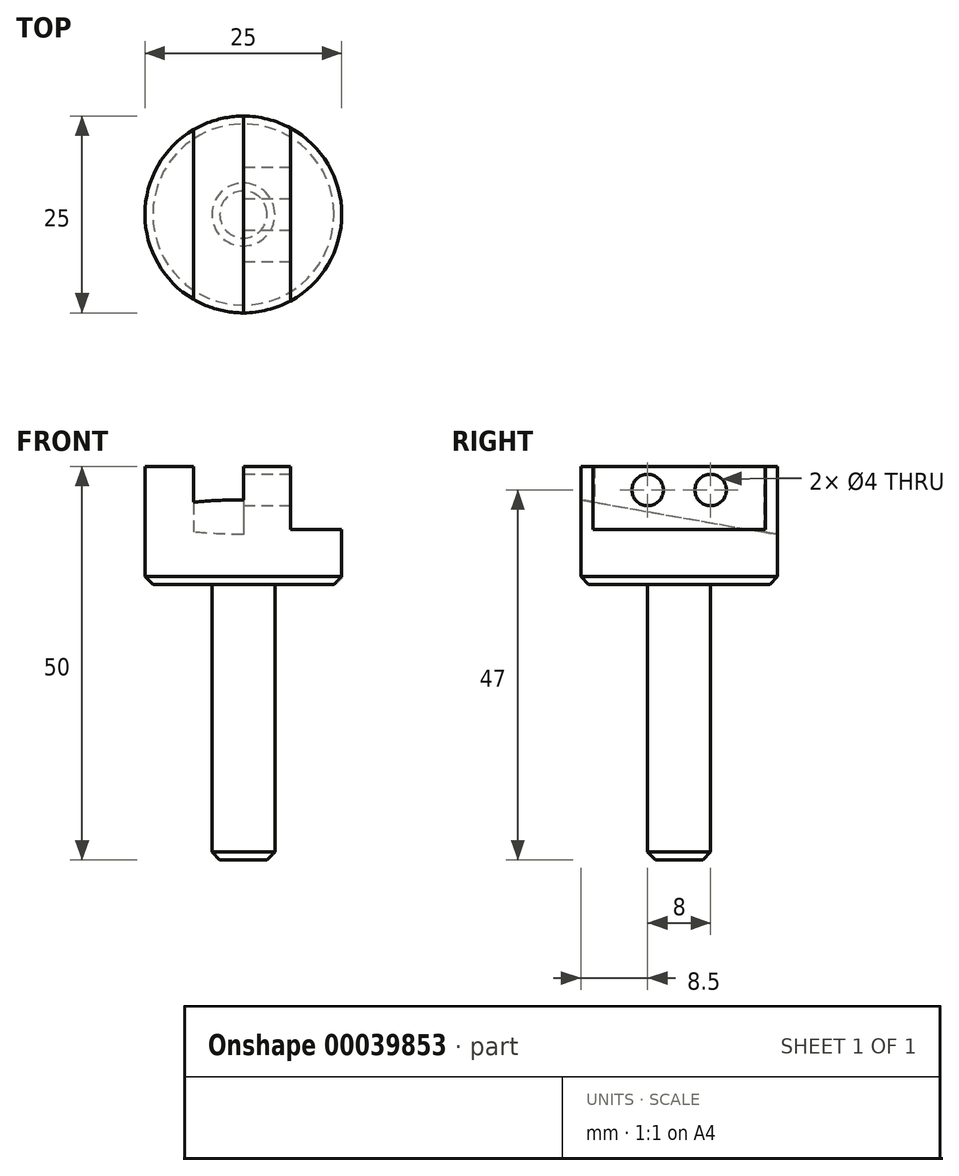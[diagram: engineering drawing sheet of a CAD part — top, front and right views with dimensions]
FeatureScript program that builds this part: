
annotation { "Feature Type Name" : "Feature", "Feature Type Description" : "" }
export const myFeature = defineFeature(function(context is Context, id is Id, definition is map)
    precondition{}
    {
        {
            var Q0;
            Q0=qCreatedBy(makeId("Top.planeOp"),FACE);
            var sketch = newSketch(context, id + "F0", { "sketchPlane" : qUnion([Q0])});
            skCircle(sketch, "E0", {"center": v(0, 0) * mm, "radius": 4 * mm});
            skSolve(sketch);
        }
        {
            var Q0;
            Q0 = qSketchRegion(id + "F0", true);
            extrude(context, id + "F1", {"entities" : qUnion([Q0]), "depth" : 35 * mm});
        }
        {
            var Q0;
            Q0=makeQuery(id+"F1.opExtrude","CAP_FACE",FACE,{"disambiguationData":[OSD([sQuery(id+"F0.wireOp",EDGE,"E0")])],"isStart":false});
            var sketch = newSketch(context, id + "F2", { "sketchPlane" : qUnion([Q0])});
            skCircle(sketch, "E1", {"center": v(0, 0) * mm, "radius": 12.5 * mm});
            skSolve(sketch);
        }
        {
            var Q0;
            Q0 = qSketchRegion(id + "F2", true);
            var Q1;
            Q1=makeQuery(id+"F2.imprint","IMPRINT",FACE,{"disambiguationData":[TD([[makeQuery(id+"F2.imprint","IMPRINT",EDGE,{"derivedFrom":sQuery(id+"F2.wireOp",EDGE,"E1")}),1.0]])]});
            extrude(context, id + "F3", {"entities" : qUnion([Q0, Q1]), "operationType" : NewBodyOperationType.ADD, "depth" : 15 * mm});
        }
        {
            var Q0;
            Q0=makeQuery(id+"F3.opExtrude","CAP_FACE",FACE,{"disambiguationData":[OSD([sQuery(id+"F2.wireOp",EDGE,"E1")])],"isStart":false});
            var sketch = newSketch(context, id + "F4", { "sketchPlane" : qUnion([Q0])});
            skCircle(sketch, "E2.cCircle", {"center": v(0, 0) * mm, "radius": 12.5 * mm, "construction": true});
            skPoint(sketch, "E3", {"position": v(0, 12.5) * mm});
            skLineSegment(sketch, "E4.MirrorCS", {"start": v(6, -10.97) * mm, "end": v(12.5, -10.97) * mm});
            skLineSegment(sketch, "E5.MirrorCS", {"start": v(6, 10.97) * mm, "end": v(12.5, 10.97) * mm});
            skLineSegment(sketch, "E6.MirrorCS", {"start": v(12.5, 10.97) * mm, "end": v(12.5, -10.97) * mm});
            skLineSegment(sketch, "E7.MirrorCS", {"start": v(6, 10.97) * mm, "end": v(6, -10.97) * mm});
            skLineSegment(sketch, "E8", {"start": v(0, 12.5) * mm, "end": v(0, 0) * mm, "construction": true});
            skSolve(sketch);
        }
        {
            var Q0;
            Q0 = qSketchRegion(id + "F4", true);
            extrude(context, id + "F5", {"entities" : qUnion([Q0]), "operationType" : NewBodyOperationType.REMOVE, "oppositeDirection" : true, "depth" : 8 * mm});
        }
        {
            var Q0;
            Q0=makeQuery(id+"F3.opExtrude","CAP_FACE",FACE,{"disambiguationData":[OSD([sQuery(id+"F2.wireOp",EDGE,"E1")])],"isStart":false});
            var sketch = newSketch(context, id + "F6", { "sketchPlane" : qUnion([Q0])});
            skLineSegment(sketch, "E9", {"start": v(6, 0) * mm, "end": v(-12.5, 0) * mm, "construction": true});
            skSolve(sketch);
        }
        {
            var Q0;
            Q0=sQuery(id+"F6.wireOp",EDGE,"E9");
            cPlane(context, id + "F7", {"entities" : qUnion([Q0]), "cplaneType" : CPlaneType.LINE_ANGLE, "offset" : 150 * mm, "angle" : 100 * degree, "width" : 150 * mm, "height" : 150 * mm});
        }
        {
            var Q0;
            Q0=qCreatedBy(id+"F7.planeOp",FACE);
            cPlane(context, id + "F8", {"entities" : qUnion([Q0]), "cplaneType" : CPlaneType.OFFSET, "offset" : 6.35 * mm, "oppositeDirection" : true, "width" : 150 * mm, "height" : 150 * mm});
        }
        {
            var Q0;
            Q0=qCreatedBy(id+"F8.planeOp",FACE);
            var sketch = newSketch(context, id + "F9", { "sketchPlane" : qUnion([Q0])});
            skPoint(sketch, "E10.rect.middle", {"position": v(0, 0) * mm});
            skLineSegment(sketch, "E11.bottom", {"start": v(0, -37.96) * mm, "end": v(-6.35, -37.96) * mm});
            skLineSegment(sketch, "E11.top", {"start": v(0, 22.04) * mm, "end": v(-6.35, 22.04) * mm});
            skLineSegment(sketch, "E11.left", {"start": v(0, -37.96) * mm, "end": v(0, 22.04) * mm});
            skLineSegment(sketch, "E11.right", {"start": v(-6.35, -37.96) * mm, "end": v(-6.35, 22.04) * mm});
            skSolve(sketch);
        }
        {
            var Q0;
            Q0 = qSketchRegion(id + "F9", true);
            extrude(context, id + "F10", {"entities" : qUnion([Q0]), "operationType" : NewBodyOperationType.REMOVE, "depth" : 25 * mm});
        }
        {
            var Q0;
            Q0=makeQuery(id+"F5.boolean.opBoolean","COPY",FACE,{"derivedFrom":makeQuery(id+"F5.opExtrude","SWEPT_FACE",FACE,{"disambiguationData":[OSD([sQuery(id+"F4.wireOp",EDGE,"E7.MirrorCS")])]})});
            var sketch = newSketch(context, id + "F11", { "sketchPlane" : qUnion([Q0])});
            skLineSegment(sketch, "E12", {"start": v(10.97, 47) * mm, "end": v(-10.97, 47) * mm, "construction": true});
            skLineSegment(sketch, "E13", {"start": v(0, 47) * mm, "end": v(0, 50) * mm, "construction": true});
            skCircle(sketch, "E14", {"center": v(4, 47) * mm, "radius": 2 * mm});
            skCircle(sketch, "E15", {"center": v(-4, 47) * mm, "radius": 2 * mm});
            skLineSegment(sketch, "E16", {"start": v(0, 47) * mm, "end": v(-4, 47) * mm, "construction": true});
            skLineSegment(sketch, "E17", {"start": v(0, 47) * mm, "end": v(4, 47) * mm, "construction": true});
            skSolve(sketch);
        }
        {
            var Q0;
            Q0 = qSketchRegion(id + "F11", true);
            extrude(context, id + "F12", {"entities" : qUnion([Q0]), "operationType" : NewBodyOperationType.REMOVE, "oppositeDirection" : true, "depth" : 8 * mm});
        }
        {
            var Q0;
            Q0=makeQuery(id+"F3.opExtrude","CAP_EDGE",EDGE,{"disambiguationData":[OSD([sQuery(id+"F2.wireOp",EDGE,"E1")])],"isStart":true});
            var Q1;
            Q1=makeQuery(id+"F1.opExtrude","CAP_EDGE",EDGE,{"disambiguationData":[OSD([sQuery(id+"F0.wireOp",EDGE,"E0")])],"isStart":true});
            chamfer(context, id + "F13", {"entities" : qUnion([Q0, Q1]), "width" : 1 * mm, "tangentPropagation" : true});
        }
    });
